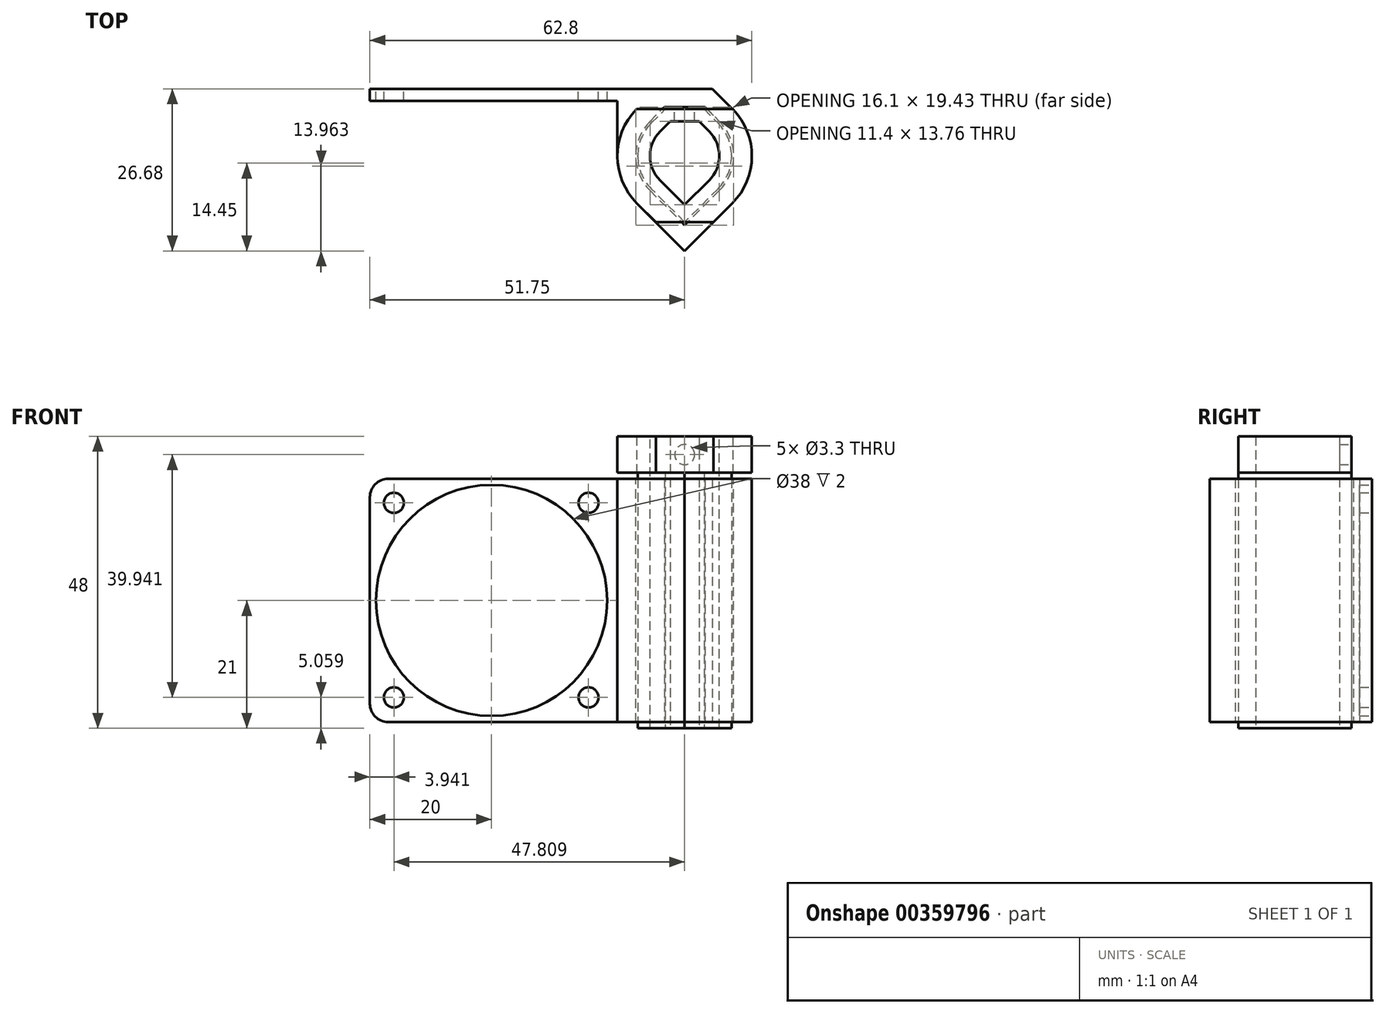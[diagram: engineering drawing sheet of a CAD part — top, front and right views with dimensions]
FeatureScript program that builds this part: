
annotation { "Feature Type Name" : "Feature", "Feature Type Description" : "" }
export const myFeature = defineFeature(function(context is Context, id is Id, definition is map)
    precondition{}
    {
        {
            var Q0;
            Q0=qCreatedBy(makeId("Front.planeOp"),FACE);
            var sketch = newSketch(context, id + "F0", { "sketchPlane" : qUnion([Q0])});
            skLineSegment(sketch, "E0.bottom", {"start": v(20, -20) * mm, "end": v(-20, -20) * mm});
            skLineSegment(sketch, "E0.top", {"start": v(20, 20) * mm, "end": v(-20, 20) * mm});
            skLineSegment(sketch, "E0.left", {"start": v(20, -20) * mm, "end": v(20, 20) * mm});
            skLineSegment(sketch, "E0.right", {"start": v(-20, -20) * mm, "end": v(-20, 20) * mm});
            skPoint(sketch, "E0.middle", {"position": v(0, 0) * mm});
            skLineSegment(sketch, "E1", {"start": v(-20, 20) * mm, "end": v(20, -20) * mm, "construction": true});
            skCircle(sketch, "E2", {"center": v(0, 0) * mm, "radius": 19 * mm});
            skPoint(sketch, "E3", {"position": v(-16.06, 16.06) * mm});
            skPoint(sketch, "E4.1.0", {"position": v(-16.06, -15.94) * mm});
            skPoint(sketch, "E4.2.0", {"position": v(15.94, -15.94) * mm});
            skPoint(sketch, "E4.3.0", {"position": v(15.94, 16.06) * mm});
            skPoint(sketch, "E4.center", {"position": v(-0.06, 0.06) * mm});
            skSolve(sketch);
        }
        {
            var Q0;
            Q0 = qSketchRegion(id + "F0", true);
            extrude(context, id + "F1", {"entities" : qUnion([Q0]), "depth" : 2 * mm});
        }
        {
            var Q0;
            Q0=sQuery(id+"F0.wireOp",VERTEX,"E3");
            var Q1;
            Q1=sQuery(id+"F0.wireOp",VERTEX,"E4.3.0");
            var Q2;
            Q2=sQuery(id+"F0.wireOp",VERTEX,"E4.2.0");
            var Q3;
            Q3=sQuery(id+"F0.wireOp",VERTEX,"E4.1.0");
            var Q4;
            Q4=makeQuery(id+"F1.opExtrude","SWEPT_BODY",BODY,{"disambiguationData":[OSD([sQuery(id+"F0.wireOp",EDGE,"E0.bottom"),sQuery(id+"F0.wireOp",EDGE,"E0.top"),sQuery(id+"F0.wireOp",EDGE,"E0.left"),sQuery(id+"F0.wireOp",EDGE,"E0.right"),sQuery(id+"F0.wireOp",EDGE,"E2")])]});
            hole(context, id + "F2", {"style" : HoleStyle.SIMPLE, "endStyle" : HoleEndStyle.THROUGH, "oppositeDirection" : true, "standardTappedOrClearance" : lookupTablePath({ "standard" : "ISO", "fit" : "Normal", "size" : "M3", "type" : "Clearance" }), "standardBlindInLast" : lookupTablePath({ "fit" : "Standard", "standard" : "ISO", "size" : "M3", "type" : "Clearance" }), "holeDiameter" : 3.3 * mm, "tappedDepth" : 12 * mm, "tapClearance" : 3, "startFromSketch" : true, "locations" : qUnion([Q0, Q1, Q2, Q3]), "scope" : qUnion([Q4])});
        }
        {
            var Q0;
            Q0=qCreatedBy(makeId("Top.planeOp"),FACE);
            var sketch = newSketch(context, id + "F3", { "sketchPlane" : qUnion([Q0])});
            skCircle(sketch, "E5.cCircle", {"center": v(31.75, -11.05) * mm, "radius": 5.35 * mm, "construction": true});
            skLineSegment(sketch, "E5.0", {"start": v(26.4, -13.27) * mm, "end": v(26.4, -8.83) * mm, "construction": true});
            skLineSegment(sketch, "E5.1", {"start": v(26.4, -8.83) * mm, "end": v(29.53, -5.7) * mm, "construction": true});
            skLineSegment(sketch, "E5.2", {"start": v(29.53, -5.7) * mm, "end": v(33.97, -5.7) * mm, "construction": true});
            skLineSegment(sketch, "E5.3", {"start": v(33.97, -5.7) * mm, "end": v(37.1, -8.83) * mm, "construction": true});
            skLineSegment(sketch, "E5.4", {"start": v(37.1, -8.83) * mm, "end": v(37.1, -13.27) * mm, "construction": true});
            skLineSegment(sketch, "E5.5", {"start": v(37.1, -13.27) * mm, "end": v(33.97, -16.4) * mm, "construction": true});
            skLineSegment(sketch, "E5.6", {"start": v(33.97, -16.4) * mm, "end": v(29.53, -16.4) * mm, "construction": true});
            skLineSegment(sketch, "E5.7", {"start": v(29.53, -16.4) * mm, "end": v(26.4, -13.27) * mm, "construction": true});
            skPoint(sketch, "E5.0.midPoint", {"position": v(26.4, -11.05) * mm});
            skLineSegment(sketch, "E6.0", {"start": v(28.7, -18.4) * mm, "end": v(24.4, -14.1) * mm, "construction": true});
            skLineSegment(sketch, "E6.1", {"start": v(34.8, -18.4) * mm, "end": v(28.7, -18.4) * mm, "construction": true});
            skLineSegment(sketch, "E6.2", {"start": v(24.4, -14.1) * mm, "end": v(24.4, -8) * mm, "construction": true});
            skLineSegment(sketch, "E6.3", {"start": v(39.1, -14.1) * mm, "end": v(34.8, -18.4) * mm, "construction": true});
            skLineSegment(sketch, "E6.4", {"start": v(24.4, -8) * mm, "end": v(28.7, -3.7) * mm, "construction": true});
            skLineSegment(sketch, "E6.5", {"start": v(28.7, -3.7) * mm, "end": v(34.8, -3.7) * mm, "construction": true});
            skLineSegment(sketch, "E6.6", {"start": v(34.8, -3.7) * mm, "end": v(39.1, -8) * mm, "construction": true});
            skLineSegment(sketch, "E6.7", {"start": v(39.1, -8) * mm, "end": v(39.1, -14.1) * mm, "construction": true});
            skLineSegment(sketch, "E7.0", {"start": v(35.08, -19.1) * mm, "end": v(28.42, -19.1) * mm, "construction": true});
            skLineSegment(sketch, "E7.1", {"start": v(39.8, -14.38) * mm, "end": v(35.08, -19.1) * mm});
            skLineSegment(sketch, "E7.2", {"start": v(28.42, -19.1) * mm, "end": v(23.7, -14.38) * mm});
            skLineSegment(sketch, "E7.3", {"start": v(39.8, -7.72) * mm, "end": v(39.8, -14.38) * mm});
            skLineSegment(sketch, "E7.4", {"start": v(23.7, -14.38) * mm, "end": v(23.7, -7.72) * mm});
            skLineSegment(sketch, "E7.5", {"start": v(23.7, -7.72) * mm, "end": v(28.42, -3) * mm});
            skLineSegment(sketch, "E7.6", {"start": v(28.42, -3) * mm, "end": v(35.08, -3) * mm});
            skLineSegment(sketch, "E7.7", {"start": v(35.08, -3) * mm, "end": v(39.8, -7.72) * mm});
            skLineSegment(sketch, "E8.0", {"start": v(27.17, -22.1) * mm, "end": v(20.7, -15.63) * mm});
            skLineSegment(sketch, "E8.1", {"start": v(36.33, -22.1) * mm, "end": v(27.17, -22.1) * mm, "construction": true});
            skLineSegment(sketch, "E8.2", {"start": v(20.7, -15.63) * mm, "end": v(20.7, -6.47) * mm});
            skLineSegment(sketch, "E8.3", {"start": v(42.8, -15.63) * mm, "end": v(36.33, -22.1) * mm});
            skLineSegment(sketch, "E8.4", {"start": v(20.7, -6.47) * mm, "end": v(27.17, 0) * mm, "construction": true});
            skLineSegment(sketch, "E8.5", {"start": v(27.17, 0) * mm, "end": v(36.33, 0) * mm});
            skLineSegment(sketch, "E8.6", {"start": v(36.33, 0) * mm, "end": v(42.8, -6.47) * mm});
            skLineSegment(sketch, "E8.7", {"start": v(42.8, -6.47) * mm, "end": v(42.8, -15.63) * mm});
            skLineSegment(sketch, "E9", {"start": v(27.17, 0) * mm, "end": v(20, 0) * mm});
            skLineSegment(sketch, "E10", {"start": v(20, 0) * mm, "end": v(20, -2) * mm});
            skLineSegment(sketch, "E11", {"start": v(20, -2) * mm, "end": v(20.7, -2) * mm});
            skLineSegment(sketch, "E12", {"start": v(20.7, -2) * mm, "end": v(20.7, -6.47) * mm});
            skLineSegment(sketch, "E13", {"start": v(28.42, -19.1) * mm, "end": v(31.75, -22.43) * mm});
            skLineSegment(sketch, "E14", {"start": v(31.75, -22.43) * mm, "end": v(35.08, -19.1) * mm});
            skLineSegment(sketch, "E15.0", {"start": v(31.75, -26.68) * mm, "end": v(37.2, -21.22) * mm, "construction": true});
            skLineSegment(sketch, "E15.1", {"start": v(26.3, -21.22) * mm, "end": v(31.75, -26.68) * mm, "construction": true});
            skLineSegment(sketch, "E16", {"start": v(27.17, -22.1) * mm, "end": v(31.75, -26.68) * mm});
            skLineSegment(sketch, "E17", {"start": v(36.33, -22.1) * mm, "end": v(31.75, -26.68) * mm});
            skSolve(sketch);
        }
        {
            var Q0;
            Q0 = qSketchRegion(id + "F3", true);
            extrude(context, id + "F4", {"entities" : qUnion([Q0]), "operationType" : NewBodyOperationType.ADD, "endBound" : BoundingType.SYMMETRIC, "depth" : 40 * mm});
        }
        {
            var Q0;
            Q0=makeQuery(id+"F4.opExtrude","SWEPT_EDGE",EDGE,{"disambiguationData":[OSD([sQuery(id+"F3.wireOp",EDGE,"E7.4"),sQuery(id+"F3.wireOp",EDGE,"E7.5")])]});
            var Q1;
            Q1=makeQuery(id+"F4.opExtrude","SWEPT_EDGE",EDGE,{"disambiguationData":[OSD([sQuery(id+"F3.wireOp",EDGE,"E7.2"),sQuery(id+"F3.wireOp",EDGE,"E7.4")])]});
            var Q2;
            Q2=makeQuery(id+"F4.opExtrude","SWEPT_EDGE",EDGE,{"disambiguationData":[OSD([sQuery(id+"F3.wireOp",EDGE,"E7.3"),sQuery(id+"F3.wireOp",EDGE,"E7.7")])]});
            var Q3;
            Q3=makeQuery(id+"F4.opExtrude","SWEPT_EDGE",EDGE,{"disambiguationData":[OSD([sQuery(id+"F3.wireOp",EDGE,"E7.1"),sQuery(id+"F3.wireOp",EDGE,"E7.3")])]});
            fillet(context, id + "F5", {"entities" : qUnion([Q0, Q1, Q2, Q3]), "radius" : 8.05 * mm, "tangentPropagation" : true, "allowEdgeOverflow" : false});
        }
        {
            var Q0;
            Q0=makeQuery(id+"F4.opExtrude","SWEPT_EDGE",EDGE,{"disambiguationData":[OSD([sQuery(id+"F3.wireOp",EDGE,"E8.0"),sQuery(id+"F3.wireOp",EDGE,"E8.2")])]});
            var Q1;
            Q1=makeQuery(id+"F4.opExtrude","SWEPT_EDGE",EDGE,{"disambiguationData":[OSD([sQuery(id+"F3.wireOp",EDGE,"E8.3"),sQuery(id+"F3.wireOp",EDGE,"E8.7")])]});
            var Q2;
            Q2=makeQuery(id+"F4.opExtrude","SWEPT_EDGE",EDGE,{"disambiguationData":[OSD([sQuery(id+"F3.wireOp",EDGE,"E8.6"),sQuery(id+"F3.wireOp",EDGE,"E8.7")])]});
            fillet(context, id + "F6", {"entities" : qUnion([Q0, Q1, Q2]), "radius" : 11.05 * mm, "tangentPropagation" : true, "allowEdgeOverflow" : false});
        }
        {
            var Q0;
            Q0=qCreatedBy(makeId("Top.planeOp"),FACE);
            var sketch = newSketch(context, id + "F7", { "sketchPlane" : qUnion([Q0])});
            skLineSegment(sketch, "E18.0", {"start": v(26.4, -13.27) * mm, "end": v(26.4, -8.83) * mm, "construction": true});
            skLineSegment(sketch, "E19.0", {"start": v(26.4, -8.83) * mm, "end": v(29.53, -5.7) * mm, "construction": true});
            skLineSegment(sketch, "E20.0", {"start": v(29.53, -5.7) * mm, "end": v(33.97, -5.7) * mm, "construction": true});
            skLineSegment(sketch, "E21.0", {"start": v(33.97, -5.7) * mm, "end": v(37.1, -8.83) * mm, "construction": true});
            skLineSegment(sketch, "E22.0", {"start": v(37.1, -8.83) * mm, "end": v(37.1, -13.27) * mm, "construction": true});
            skLineSegment(sketch, "E23.0", {"start": v(34.8, -3.7) * mm, "end": v(39.1, -8) * mm, "construction": true});
            skLineSegment(sketch, "E24.0", {"start": v(39.1, -8) * mm, "end": v(39.1, -14.1) * mm, "construction": true});
            skLineSegment(sketch, "E25.0", {"start": v(24.4, -14.1) * mm, "end": v(24.4, -8) * mm, "construction": true});
            skLineSegment(sketch, "E26.0", {"start": v(24.4, -8) * mm, "end": v(28.7, -3.7) * mm, "construction": true});
            skLineSegment(sketch, "E27.0", {"start": v(28.7, -3.7) * mm, "end": v(34.8, -3.7) * mm, "construction": true});
            skLineSegment(sketch, "E28", {"start": v(26.4, -13.27) * mm, "end": v(31.75, -18.62) * mm, "construction": true});
            skPoint(sketch, "E28.endSnap0", {"position": v(31.75, -5.7) * mm});
            skLineSegment(sketch, "E29", {"start": v(31.75, -18.62) * mm, "end": v(37.1, -13.27) * mm, "construction": true});
            skLineSegment(sketch, "E30", {"start": v(39.1, -14.1) * mm, "end": v(31.75, -21.44) * mm, "construction": true});
            skLineSegment(sketch, "E31", {"start": v(31.75, -21.44) * mm, "end": v(24.4, -14.1) * mm, "construction": true});
            skLineSegment(sketch, "E32.0", {"start": v(24.05, -14.24) * mm, "end": v(24.05, -7.86) * mm});
            skLineSegment(sketch, "E32.1", {"start": v(31.75, -21.94) * mm, "end": v(24.05, -14.24) * mm});
            skLineSegment(sketch, "E32.2", {"start": v(28.56, -3.35) * mm, "end": v(34.94, -3.35) * mm});
            skLineSegment(sketch, "E32.3", {"start": v(34.94, -3.35) * mm, "end": v(39.45, -7.86) * mm});
            skLineSegment(sketch, "E32.4", {"start": v(39.45, -7.86) * mm, "end": v(39.45, -14.24) * mm});
            skLineSegment(sketch, "E32.5", {"start": v(24.05, -7.86) * mm, "end": v(28.56, -3.35) * mm});
            skLineSegment(sketch, "E32.6", {"start": v(39.45, -14.24) * mm, "end": v(31.75, -21.94) * mm});
            skLineSegment(sketch, "E33.0", {"start": v(26.05, -13.41) * mm, "end": v(26.05, -8.69) * mm});
            skLineSegment(sketch, "E33.1", {"start": v(26.05, -8.69) * mm, "end": v(29.39, -5.35) * mm});
            skLineSegment(sketch, "E33.2", {"start": v(31.75, -19.11) * mm, "end": v(37.45, -13.41) * mm});
            skLineSegment(sketch, "E33.3", {"start": v(37.45, -8.69) * mm, "end": v(37.45, -13.41) * mm});
            skLineSegment(sketch, "E33.4", {"start": v(34.11, -5.35) * mm, "end": v(37.45, -8.69) * mm});
            skLineSegment(sketch, "E33.5", {"start": v(26.05, -13.41) * mm, "end": v(31.75, -19.11) * mm});
            skLineSegment(sketch, "E33.6", {"start": v(29.39, -5.35) * mm, "end": v(34.11, -5.35) * mm});
            skSolve(sketch);
        }
        {
            var Q0;
            Q0 = qSketchRegion(id + "F7", true);
            extrude(context, id + "F8", {"entities" : qUnion([Q0]), "endBound" : BoundingType.SYMMETRIC, "depth" : 42 * mm});
        }
        {
            var Q0;
            Q0=makeQuery(id+"F8.opExtrude","SWEPT_EDGE",EDGE,{"disambiguationData":[OSD([sQuery(id+"F7.wireOp",EDGE,"E32.4"),sQuery(id+"F7.wireOp",EDGE,"E32.6")])]});
            var Q1;
            Q1=makeQuery(id+"F8.opExtrude","SWEPT_EDGE",EDGE,{"disambiguationData":[OSD([sQuery(id+"F7.wireOp",EDGE,"E32.3"),sQuery(id+"F7.wireOp",EDGE,"E32.4")])]});
            var Q2;
            Q2=makeQuery(id+"F8.opExtrude","SWEPT_EDGE",EDGE,{"disambiguationData":[OSD([sQuery(id+"F7.wireOp",EDGE,"E32.0"),sQuery(id+"F7.wireOp",EDGE,"E32.1")])]});
            var Q3;
            Q3=makeQuery(id+"F8.opExtrude","SWEPT_EDGE",EDGE,{"disambiguationData":[OSD([sQuery(id+"F7.wireOp",EDGE,"E32.0"),sQuery(id+"F7.wireOp",EDGE,"E32.5")])]});
            fillet(context, id + "F9", {"entities" : qUnion([Q0, Q1, Q2, Q3]), "radius" : 7.55 * mm, "tangentPropagation" : true, "allowEdgeOverflow" : false});
        }
        {
            var Q0;
            Q0=makeQuery(id+"F8.opExtrude","SWEPT_EDGE",EDGE,{"disambiguationData":[OSD([sQuery(id+"F7.wireOp",EDGE,"E33.3"),sQuery(id+"F7.wireOp",EDGE,"E33.4")])]});
            var Q1;
            Q1=makeQuery(id+"F8.opExtrude","SWEPT_EDGE",EDGE,{"disambiguationData":[OSD([sQuery(id+"F7.wireOp",EDGE,"E33.2"),sQuery(id+"F7.wireOp",EDGE,"E33.3")])]});
            var Q2;
            Q2=makeQuery(id+"F8.opExtrude","SWEPT_EDGE",EDGE,{"disambiguationData":[OSD([sQuery(id+"F7.wireOp",EDGE,"E33.0"),sQuery(id+"F7.wireOp",EDGE,"E33.1")])]});
            var Q3;
            Q3=makeQuery(id+"F8.opExtrude","SWEPT_EDGE",EDGE,{"disambiguationData":[OSD([sQuery(id+"F7.wireOp",EDGE,"E33.0"),sQuery(id+"F7.wireOp",EDGE,"E33.5")])]});
            fillet(context, id + "F10", {"entities" : qUnion([Q0, Q1, Q2, Q3]), "radius" : 5.7 * mm, "tangentPropagation" : true, "allowEdgeOverflow" : false});
        }
        {
            var Q0;
            Q0=makeQuery(id+"F8.opExtrude","CAP_FACE",FACE,{"disambiguationData":[OSD([sQuery(id+"F7.wireOp",EDGE,"E32.0"),sQuery(id+"F7.wireOp",EDGE,"E32.1"),sQuery(id+"F7.wireOp",EDGE,"E32.2"),sQuery(id+"F7.wireOp",EDGE,"E32.3"),sQuery(id+"F7.wireOp",EDGE,"E32.4"),sQuery(id+"F7.wireOp",EDGE,"E32.5"),sQuery(id+"F7.wireOp",EDGE,"E32.6"),sQuery(id+"F7.wireOp",EDGE,"E33.0"),sQuery(id+"F7.wireOp",EDGE,"E33.1"),sQuery(id+"F7.wireOp",EDGE,"E33.2"),sQuery(id+"F7.wireOp",EDGE,"E33.3"),sQuery(id+"F7.wireOp",EDGE,"E33.4"),sQuery(id+"F7.wireOp",EDGE,"E33.5"),sQuery(id+"F7.wireOp",EDGE,"E33.6")])],"isStart":false});
            var sketch = newSketch(context, id + "F11", { "sketchPlane" : qUnion([Q0])});
            skArc(sketch, "E34.0", {"start": v(23.94, -18.86) * mm, "mid": v(20.7, -11.13) * mm, "end": v(23.82, -3.35) * mm});
            skArc(sketch, "E35.0", {"start": v(39.56, -18.86) * mm, "mid": v(42.8, -11.13) * mm, "end": v(39.68, -3.35) * mm});
            skLineSegment(sketch, "E36", {"start": v(23.82, -3.35) * mm, "end": v(39.68, -3.35) * mm});
            skLineSegment(sketch, "E37.0", {"start": v(27.01, -21.94) * mm, "end": v(23.94, -18.86) * mm});
            skLineSegment(sketch, "E38.0", {"start": v(39.56, -18.86) * mm, "end": v(36.49, -21.94) * mm});
            skLineSegment(sketch, "E39", {"start": v(27.01, -21.94) * mm, "end": v(36.49, -21.94) * mm});
            skPoint(sketch, "E40.orphan", {"position": v(31.75, -26.68) * mm});
            skLineSegment(sketch, "E41.0", {"start": v(29.39, -5.35) * mm, "end": v(34.11, -5.35) * mm});
            skLineSegment(sketch, "E42.0", {"start": v(34.11, -5.35) * mm, "end": v(35.78, -7.02) * mm});
            skArc(sketch, "E43.0", {"start": v(35.78, -7.02) * mm, "mid": v(37.45, -11.05) * mm, "end": v(35.78, -15.08) * mm});
            skLineSegment(sketch, "E44.0", {"start": v(31.75, -19.11) * mm, "end": v(35.78, -15.08) * mm});
            skLineSegment(sketch, "E45.0", {"start": v(27.72, -15.08) * mm, "end": v(31.75, -19.11) * mm});
            skArc(sketch, "E46.0", {"start": v(27.72, -15.08) * mm, "mid": v(26.05, -11.05) * mm, "end": v(27.72, -7.02) * mm});
            skLineSegment(sketch, "E47.0", {"start": v(27.72, -7.02) * mm, "end": v(29.39, -5.35) * mm});
            skSolve(sketch);
        }
        {
            var Q0;
            Q0 = qSketchRegion(id + "F11", true);
            extrude(context, id + "F12", {"entities" : qUnion([Q0]), "operationType" : NewBodyOperationType.ADD, "depth" : 6 * mm});
        }
        {
            var Q0;
            Q0=makeQuery(id+"F12.boolean.opBoolean","MERGE",FACE,{"derivedFrom":[makeQuery(id+"F8.opExtrude","SWEPT_FACE",FACE,{"disambiguationData":[OSD([sQuery(id+"F7.wireOp",EDGE,"E32.2")])]}),makeQuery(id+"F12.opExtrude","SWEPT_FACE",FACE,{"disambiguationData":[OSD([sQuery(id+"F11.wireOp",EDGE,"E36")])]})]});
            var sketch = newSketch(context, id + "F13", { "sketchPlane" : qUnion([Q0])});
            skLineSegment(sketch, "E48", {"start": v(-31.75, 27) * mm, "end": v(-31.75, 21) * mm, "construction": true});
            skCircle(sketch, "E49", {"center": v(-31.75, 24) * mm, "radius": 1.65 * mm});
            skSolve(sketch);
        }
        {
            var Q0;
            Q0 = qSketchRegion(id + "F13", true);
            extrude(context, id + "F14", {"entities" : qUnion([Q0]), "operationType" : NewBodyOperationType.REMOVE, "oppositeDirection" : true, "depth" : 5 * mm});
        }
        {
            var Q0;
            Q0=makeQuery(id+"F1.opExtrude","SWEPT_EDGE",EDGE,{"disambiguationData":[OSD([sQuery(id+"F0.wireOp",EDGE,"E0.top"),sQuery(id+"F0.wireOp",EDGE,"E0.right")])]});
            var Q1;
            Q1=makeQuery(id+"F1.opExtrude","SWEPT_EDGE",EDGE,{"disambiguationData":[OSD([sQuery(id+"F0.wireOp",EDGE,"E0.bottom"),sQuery(id+"F0.wireOp",EDGE,"E0.right")])]});
            fillet(context, id + "F15", {"entities" : qUnion([Q0, Q1]), "radius" : 3 * mm, "tangentPropagation" : true, "allowEdgeOverflow" : false});
        }
    });
